# Revit family: BT4-200
name_source: partatom
category: Structural Connections
revit_build: Autodesk Revit 2015 (Build: 20140606_1530(x64)
units: mm (PartAtom-declared; Revit-internal decimal feet)

## types (1)
- BT4-200
    Default Elevation = 0 mm  [stored 0 ft]
    Density = 1.18 kg
    Description = Concealed beam hanger
    EPD = https://www.strongtie.eu
    ETA / DoP = https://www.strongtie.eu
    Manufacturer = Simpson Strong-Tie
    Model = BT4-200
    Model Disclaimer = Contact Simpson Strong-Tie Company  for more information
    Model ID = 0154826900457665381524055049848849694008
    Name = BT4-200
    ObjectType = BT4-200
    Product Material = Galvanised
    Product Type = Concealed beam hanger
    Reference = BT4-200
    STD type1 = STD12X60
    STD type2 = STD12X80
    STD type3 = STD12X100
    STD type4 = STD12X120
    STD type5 = STD12X140
    STD type6 = STD12X160
    Technical datasheet = https://www.strongtie.eu
    URL = www.strongtie.eu
    UniClass Number = Pr_20_29_31_13
    UniClass Title = Carbon steel punched metal plate fasteners

note: [stored X ft] marks values corroborated as IEEE doubles in the binary element streams (Revit-internal decimal feet)

## geometry (parser evidence)
native form markers: Blend x58, Sweep x11
no freeform markers — native parametric forms only
